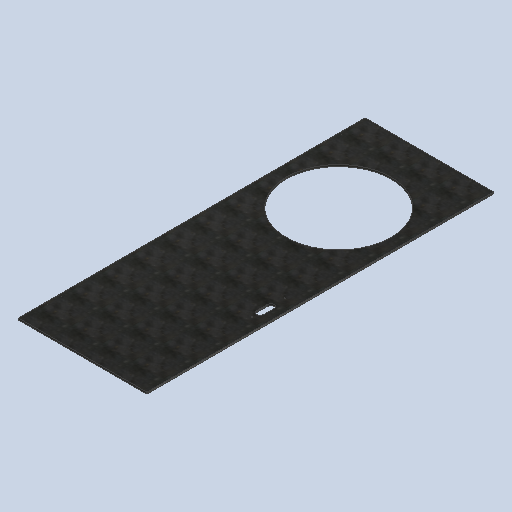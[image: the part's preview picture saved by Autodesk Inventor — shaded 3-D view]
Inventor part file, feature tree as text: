
AUTODESK INVENTOR PART (.ipt)
format: ipt  version: 2025.1 (Build 291241000, 241)  size: 340,480 bytes
history: native  units: mm
features: other x3, sketch x1, plane x1
ambient origin geometry x8: Origin, YZ Plane, XZ Plane, XY Plane, X Axis, Y Axis, Z Axis, Center Point
bodies: Solid1 (feature_tree)
feature tree (5):
  other  "Rahmen.ipt"
  other  "Solid1::Rahmen.ipt"
  other  "TaggingFeature1"
  sketch  "Sketch7"  dims[d0=10.0mm]
  plane  "Work Plane1"
